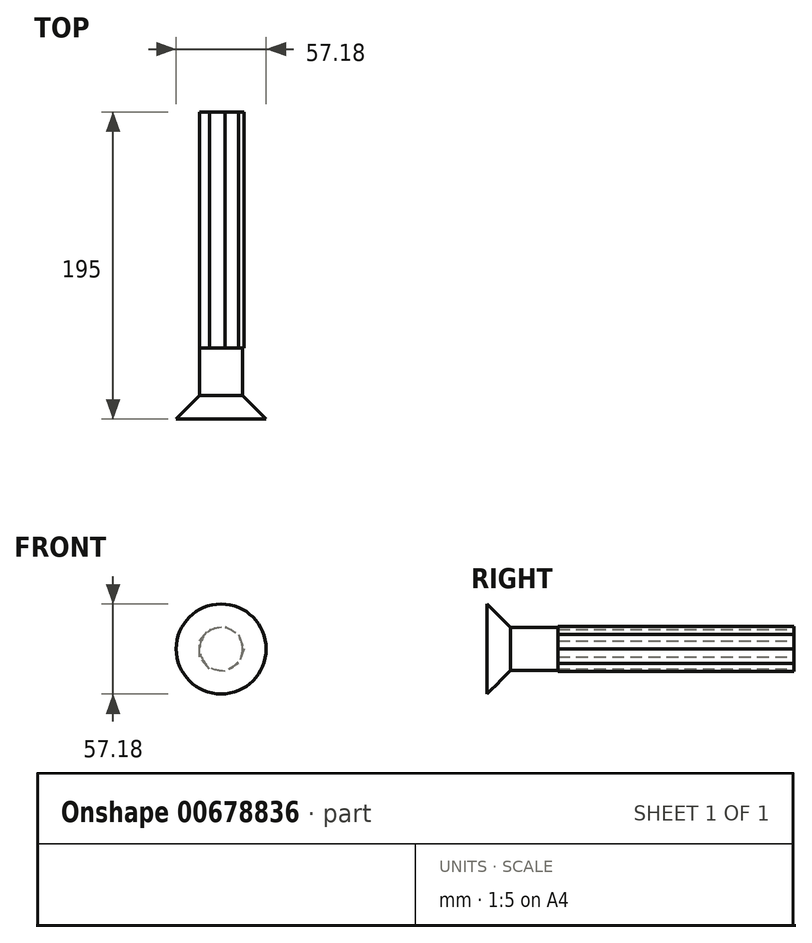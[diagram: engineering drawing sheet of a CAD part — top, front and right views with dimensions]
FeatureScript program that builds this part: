
annotation { "Feature Type Name" : "Feature", "Feature Type Description" : "" }
export const myFeature = defineFeature(function(context is Context, id is Id, definition is map)
    precondition{}
    {
        {
            var Q0;
            Q0=qCreatedBy(makeId("Front.planeOp"),FACE);
            var sketch = newSketch(context, id + "F0", { "sketchPlane" : qUnion([Q0])});
            skLineSegment(sketch, "E0.0", {"start": v(-13.63, -4.96) * mm, "end": v(-13.63, 4.96) * mm});
            skLineSegment(sketch, "E0.1", {"start": v(-13.63, 4.96) * mm, "end": v(-7.25, 12.57) * mm});
            skLineSegment(sketch, "E0.2", {"start": v(-7.25, 12.57) * mm, "end": v(2.52, 14.29) * mm});
            skLineSegment(sketch, "E0.3", {"start": v(2.52, 14.29) * mm, "end": v(11.11, 9.33) * mm});
            skLineSegment(sketch, "E0.4", {"start": v(11.11, 9.33) * mm, "end": v(14.5, 0) * mm});
            skLineSegment(sketch, "E0.5", {"start": v(14.5, 0) * mm, "end": v(11.11, -9.33) * mm});
            skLineSegment(sketch, "E0.6", {"start": v(11.11, -9.33) * mm, "end": v(2.52, -14.29) * mm});
            skLineSegment(sketch, "E0.7", {"start": v(2.52, -14.29) * mm, "end": v(-7.25, -12.57) * mm});
            skLineSegment(sketch, "E0.8", {"start": v(-7.25, -12.57) * mm, "end": v(-13.63, -4.96) * mm});
            skSolve(sketch);
        }
        {
            var Q0;
            Q0=makeQuery(id+"F0.imprint","IMPRINT",FACE,{"disambiguationData":[TD([[makeQuery(id+"F0.imprint","IMPRINT",EDGE,{"derivedFrom":sQuery(id+"F0.wireOp",EDGE,"E0.0")}),-1.0]])]});
            extrude(context, id + "F1", {"entities" : qUnion([Q0]), "depth" : 150 * mm, "offsetDistance" : 25 * mm});
        }
        {
            var Q0;
            Q0=makeQuery(id+"F1.opExtrude","CAP_FACE",FACE,{"disambiguationData":[OSD([sQuery(id+"F0.wireOp",EDGE,"E0.0"),sQuery(id+"F0.wireOp",EDGE,"E0.1"),sQuery(id+"F0.wireOp",EDGE,"E0.2"),sQuery(id+"F0.wireOp",EDGE,"E0.3"),sQuery(id+"F0.wireOp",EDGE,"E0.4"),sQuery(id+"F0.wireOp",EDGE,"E0.5"),sQuery(id+"F0.wireOp",EDGE,"E0.6"),sQuery(id+"F0.wireOp",EDGE,"E0.7"),sQuery(id+"F0.wireOp",EDGE,"E0.8")])],"isStart":false});
            var sketch = newSketch(context, id + "F2", { "sketchPlane" : qUnion([Q0])});
            skCircle(sketch, "E1", {"center": v(0, 0) * mm, "radius": 13.59 * mm});
            skSolve(sketch);
        }
        {
            var Q0;
            Q0=makeQuery(id+"F2.imprint","IMPRINT",FACE,{"disambiguationData":[TD([[makeQuery(id+"F2.imprint","IMPRINT",EDGE,{"derivedFrom":sQuery(id+"F2.wireOp",EDGE,"E1")}),1.0]])]});
            extrude(context, id + "F3", {"entities" : qUnion([Q0]), "operationType" : NewBodyOperationType.ADD, "depth" : 30 * mm, "offsetDistance" : 25 * mm});
        }
        {
            var Q0;
            Q0=makeQuery(id+"F3.opExtrude","CAP_FACE",FACE,{"disambiguationData":[OSD([sQuery(id+"F2.wireOp",EDGE,"E1")])],"isStart":false});
            extrude(context, id + "F4", {"entities" : qUnion([Q0]), "operationType" : NewBodyOperationType.ADD, "depth" : 15 * mm, "offsetDistance" : 25 * mm, "hasDraft" : true, "draftAngle" : 45 * degree});
        }
    });
